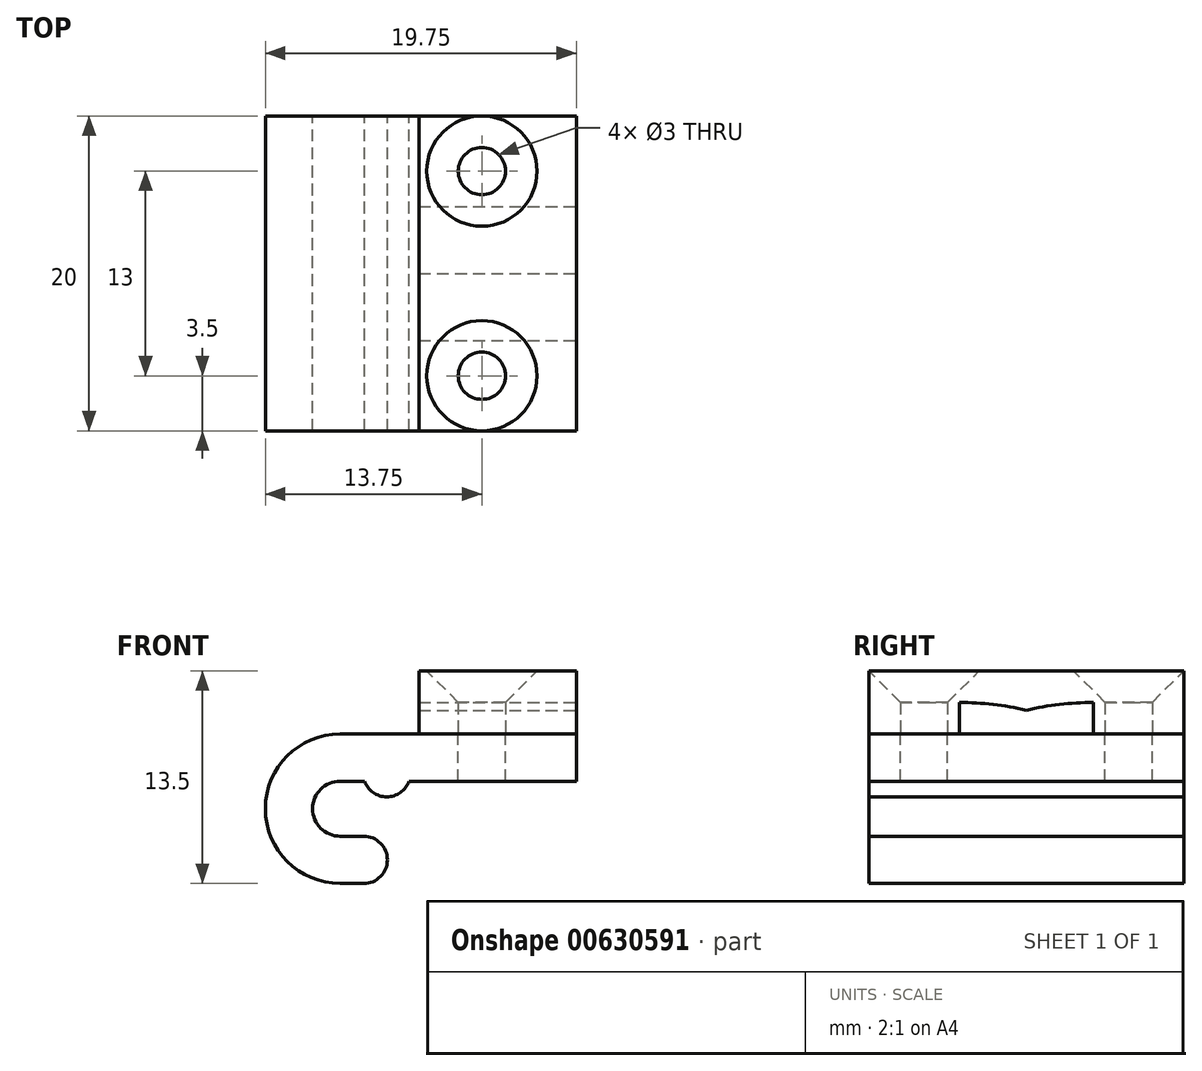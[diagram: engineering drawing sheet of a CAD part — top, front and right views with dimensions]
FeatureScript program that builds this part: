
annotation { "Feature Type Name" : "Feature", "Feature Type Description" : "" }
export const myFeature = defineFeature(function(context is Context, id is Id, definition is map)
    precondition{}
    {
        {
            var Q0;
            Q0=qCreatedBy(makeId("Front.planeOp"),FACE);
            var sketch = newSketch(context, id + "F0", { "sketchPlane" : qUnion([Q0])});
            skArc(sketch, "E0", {"start": v(0, 1.75) * mm, "mid": v(-1.75, 0) * mm, "end": v(0, -1.75) * mm});
            skArc(sketch, "E1", {"start": v(0, 4.75) * mm, "mid": v(-4.75, 0) * mm, "end": v(0, -4.75) * mm});
            skLineSegment(sketch, "E2", {"start": v(15, 4.75) * mm, "end": v(15, 1.75) * mm});
            skPoint(sketch, "E3.visualSharp", {"position": v(1.73, 0.24) * mm});
            skLineSegment(sketch, "E3.filletArc", {"start": v(0, 1.75) * mm, "end": v(0, 1.75) * mm});
            skPoint(sketch, "E4.visualSharp", {"position": v(3.68, 3) * mm});
            skLineSegment(sketch, "E5", {"start": v(0, 4.75) * mm, "end": v(15, 4.75) * mm});
            skLineSegment(sketch, "E6", {"start": v(0, 1.75) * mm, "end": v(15, 1.75) * mm});
            skLineSegment(sketch, "E7", {"start": v(0, -1.75) * mm, "end": v(1.5, -1.75) * mm});
            skLineSegment(sketch, "E8", {"start": v(0, -4.75) * mm, "end": v(1.5, -4.75) * mm});
            skArc(sketch, "E9", {"start": v(1.5, -4.75) * mm, "mid": v(3, -3.25) * mm, "end": v(1.5, -1.75) * mm});
            skCircle(sketch, "E10", {"center": v(0, 0) * mm, "radius": 1.5 * mm, "construction": true});
            skArc(sketch, "E11", {"start": v(1.54, 1.75) * mm, "mid": v(2.96, 0.75) * mm, "end": v(4.37, 1.75) * mm});
            skSolve(sketch);
        }
        {
            var Q0;
            Q0=makeQuery(id+"F0.imprint","IMPRINT",FACE,{"disambiguationData":[TD([[makeQuery(id+"F0.imprint","IMPRINT",EDGE,{"derivedFrom":sQuery(id+"F0.wireOp",EDGE,"E0")}),-1.0]])]});
            var Q1;
            {var subQ0=sQuery(id+"F0.wireOp",EDGE,"E11");Q1=makeQuery(id+"F0.imprint","IMPRINT",FACE,{"disambiguationData":[TD([[makeQuery(id+"F0.imprint","IMPRINT",EDGE,{"derivedFrom":subQ0}),1.0]])]});}
            extrude(context, id + "F1", {"entities" : qUnion([Q0, Q1]), "depth" : 20 * mm, "offsetDistance" : 25 * mm});
        }
        {
            var Q0;
            Q0=makeQuery(id+"F1.opExtrude","SWEPT_FACE",FACE,{"disambiguationData":[OSD([sQuery(id+"F0.wireOp",EDGE,"E5")])]});
            var sketch = newSketch(context, id + "F2", { "sketchPlane" : qUnion([Q0])});
            skLineSegment(sketch, "E12.0.0", {"start": v(15, 0) * mm, "end": v(0, 0) * mm});
            skLineSegment(sketch, "E12.0.1", {"start": v(0, 0) * mm, "end": v(0, -20) * mm});
            skLineSegment(sketch, "E12.0.2", {"start": v(0, -20) * mm, "end": v(15, -20) * mm});
            skLineSegment(sketch, "E12.0.3", {"start": v(15, -20) * mm, "end": v(15, 0) * mm});
            skCircle(sketch, "E13", {"center": v(9, -3.5) * mm, "radius": 1.5 * mm});
            skCircle(sketch, "E14", {"center": v(9, -16.5) * mm, "radius": 1.5 * mm});
            skLineSegment(sketch, "E15", {"start": v(9, -3.5) * mm, "end": v(9, 0) * mm, "construction": true});
            skLineSegment(sketch, "E16", {"start": v(9, -16.5) * mm, "end": v(9, -20) * mm, "construction": true});
            skSolve(sketch);
        }
        {
            var Q0;
            Q0=makeQuery(id+"F2.imprint","IMPRINT",FACE,{"disambiguationData":[TD([[makeQuery(id+"F2.imprint","IMPRINT",EDGE,{"derivedFrom":sQuery(id+"F2.wireOp",EDGE,"E13")}),1.0]])]});
            var Q1;
            Q1=makeQuery(id+"F2.imprint","IMPRINT",FACE,{"disambiguationData":[TD([[makeQuery(id+"F2.imprint","IMPRINT",EDGE,{"derivedFrom":sQuery(id+"F2.wireOp",EDGE,"E14")}),1.0]])]});
            extrude(context, id + "F3", {"entities" : qUnion([Q0, Q1]), "operationType" : NewBodyOperationType.REMOVE, "endBound" : BoundingType.THROUGH_ALL, "oppositeDirection" : true, "depth" : 25 * mm, "offsetDistance" : 25 * mm});
        }
        {
            var Q0;
            Q0=makeQuery(id+"F1.opExtrude","SWEPT_FACE",FACE,{"disambiguationData":[OSD([sQuery(id+"F0.wireOp",EDGE,"E5")])]});
            var sketch = newSketch(context, id + "F4", { "sketchPlane" : qUnion([Q0])});
            skLineSegment(sketch, "E17", {"start": v(15, 0) * mm, "end": v(5, 0) * mm});
            skLineSegment(sketch, "E18", {"start": v(5, -20) * mm, "end": v(15, -20) * mm});
            skLineSegment(sketch, "E19", {"start": v(5, -5.75) * mm, "end": v(15, -5.75) * mm});
            skLineSegment(sketch, "E20", {"start": v(5, -14.25) * mm, "end": v(15, -14.25) * mm});
            skLineSegment(sketch, "E21", {"start": v(5, -5.75) * mm, "end": v(5, 0) * mm});
            skLineSegment(sketch, "E22", {"start": v(5, -14.25) * mm, "end": v(5, -20) * mm});
            skLineSegment(sketch, "E23", {"start": v(15, 0) * mm, "end": v(15, -5.75) * mm});
            skLineSegment(sketch, "E24", {"start": v(15, -14.25) * mm, "end": v(15, -20) * mm});
            skSolve(sketch);
        }
        {
            var Q0;
            Q0=makeQuery(id+"F4.imprint","IMPRINT",FACE,{"disambiguationData":[TD([[makeQuery(id+"F4.imprint","IMPRINT",EDGE,{"derivedFrom":sQuery(id+"F4.wireOp",EDGE,"E17")}),-1.0]])]});
            var Q1;
            Q1=makeQuery(id+"F4.imprint","IMPRINT",FACE,{"disambiguationData":[TD([[makeQuery(id+"F4.imprint","IMPRINT",EDGE,{"derivedFrom":sQuery(id+"F4.wireOp",EDGE,"E18")}),1.0]])]});
            extrude(context, id + "F5", {"entities" : qUnion([Q0, Q1]), "depth" : 2 * mm, "offsetDistance" : 25 * mm});
        }
        {
            var Q0;
            Q0=makeQuery(id+"F5.opExtrude","CAP_FACE",FACE,{"disambiguationData":[OSD([sQuery(id+"F2.wireOp",EDGE,"E13"),sQuery(id+"F4.wireOp",EDGE,"E17"),sQuery(id+"F4.wireOp",EDGE,"E19"),sQuery(id+"F4.wireOp",EDGE,"E21"),sQuery(id+"F4.wireOp",EDGE,"E23")])],"isStart":false});
            var sketch = newSketch(context, id + "F6", { "sketchPlane" : qUnion([Q0])});
            skPoint(sketch, "E25.0", {"position": v(5, 0) * mm});
            skPoint(sketch, "E26.0", {"position": v(15, 0) * mm});
            skPoint(sketch, "E27.0", {"position": v(15, -20) * mm});
            skPoint(sketch, "E28.0", {"position": v(5, -20) * mm});
            skCircle(sketch, "E29.0", {"center": v(9, -16.5) * mm, "radius": 1.5 * mm});
            skCircle(sketch, "E30.0", {"center": v(9, -3.5) * mm, "radius": 1.5 * mm});
            skLineSegment(sketch, "E31.bottom", {"start": v(5, 0) * mm, "end": v(15, 0) * mm});
            skLineSegment(sketch, "E31.top", {"start": v(5, -20) * mm, "end": v(15, -20) * mm});
            skLineSegment(sketch, "E31.left", {"start": v(5, 0) * mm, "end": v(5, -20) * mm});
            skLineSegment(sketch, "E31.right", {"start": v(15, 0) * mm, "end": v(15, -20) * mm});
            skSolve(sketch);
        }
        {
            var Q0;
            Q0=makeQuery(id+"F6.imprint","IMPRINT",FACE,{"disambiguationData":[TD([[makeQuery(id+"F6.imprint","IMPRINT",EDGE,{"derivedFrom":sQuery(id+"F6.wireOp",EDGE,"E30.0")}),-1.0]])]});
            var Q1;
            Q1=makeQuery(id+"F6.imprint","IMPRINT",FACE,{"disambiguationData":[TD([[makeQuery(id+"F6.imprint","IMPRINT",EDGE,{"derivedFrom":sQuery(id+"F6.wireOp",EDGE,"E29.0")}),-1.0]])]});
            extrude(context, id + "F7", {"entities" : qUnion([Q0, Q1]), "operationType" : NewBodyOperationType.ADD, "depth" : 2 * mm, "offsetDistance" : 25 * mm});
        }
        {
            var Q0;
            Q0=makeQuery(id+"F7.opExtrude","CAP_EDGE",EDGE,{"disambiguationData":[OSD([sQuery(id+"F6.wireOp",EDGE,"E29.0")])],"isStart":false});
            var Q1;
            Q1=makeQuery(id+"F7.opExtrude","CAP_EDGE",EDGE,{"disambiguationData":[OSD([sQuery(id+"F6.wireOp",EDGE,"E30.0")])],"isStart":false});
            chamfer(context, id + "F8", {"entities" : qUnion([Q0, Q1]), "width" : 2 * mm, "tangentPropagation" : true});
        }
        {
            var Q0;
            Q0=makeQuery(id+"F7.boolean.opBoolean","MERGE",FACE,{"derivedFrom":[makeQuery(id+"F5.opExtrude","SWEPT_FACE",FACE,{"disambiguationData":[OSD([sQuery(id+"F4.wireOp",EDGE,"E23")])]}),makeQuery(id+"F5.opExtrude","SWEPT_FACE",FACE,{"disambiguationData":[OSD([sQuery(id+"F4.wireOp",EDGE,"E24")])]}),makeQuery(id+"F7.opExtrude","SWEPT_FACE",FACE,{"disambiguationData":[OSD([sQuery(id+"F6.wireOp",EDGE,"E31.right")])]})]});
            var sketch = newSketch(context, id + "F9", { "sketchPlane" : qUnion([Q0])});
            skLineSegment(sketch, "E32.0", {"start": v(-14.25, 6.75) * mm, "end": v(-5.75, 6.75) * mm});
            skLineSegment(sketch, "E33", {"start": v(-10, 6.75) * mm, "end": v(-10, 6.25) * mm, "construction": true});
            skArc(sketch, "E34", {"start": v(-10, 6.25) * mm, "mid": v(-12.11, 6.62) * mm, "end": v(-14.25, 6.75) * mm});
            skArc(sketch, "E35", {"start": v(-5.75, 6.75) * mm, "mid": v(-7.89, 6.62) * mm, "end": v(-10, 6.25) * mm});
            skSolve(sketch);
        }
        {
            var Q0;
            Q0=makeQuery(id+"F9.imprint","IMPRINT",FACE,{"disambiguationData":[TD([[makeQuery(id+"F9.imprint","IMPRINT",EDGE,{"derivedFrom":sQuery(id+"F9.wireOp",EDGE,"E32.0")}),-1.0]])]});
            var Q1;
            Q1=makeQuery(id+"F7.boolean.opBoolean","MERGE",FACE,{"derivedFrom":[makeQuery(id+"F5.opExtrude","SWEPT_FACE",FACE,{"disambiguationData":[OSD([sQuery(id+"F4.wireOp",EDGE,"E21")])]}),makeQuery(id+"F5.opExtrude","SWEPT_FACE",FACE,{"disambiguationData":[OSD([sQuery(id+"F4.wireOp",EDGE,"E22")])]}),makeQuery(id+"F7.opExtrude","SWEPT_FACE",FACE,{"disambiguationData":[OSD([sQuery(id+"F6.wireOp",EDGE,"E31.left")])]})]});
            extrude(context, id + "F10", {"entities" : qUnion([Q0]), "operationType" : NewBodyOperationType.ADD, "endBound" : BoundingType.UP_TO_SURFACE, "oppositeDirection" : true, "depth" : 25 * mm, "endBoundEntityFace" : qUnion([Q1]), "offsetDistance" : 25 * mm});
        }
    });
